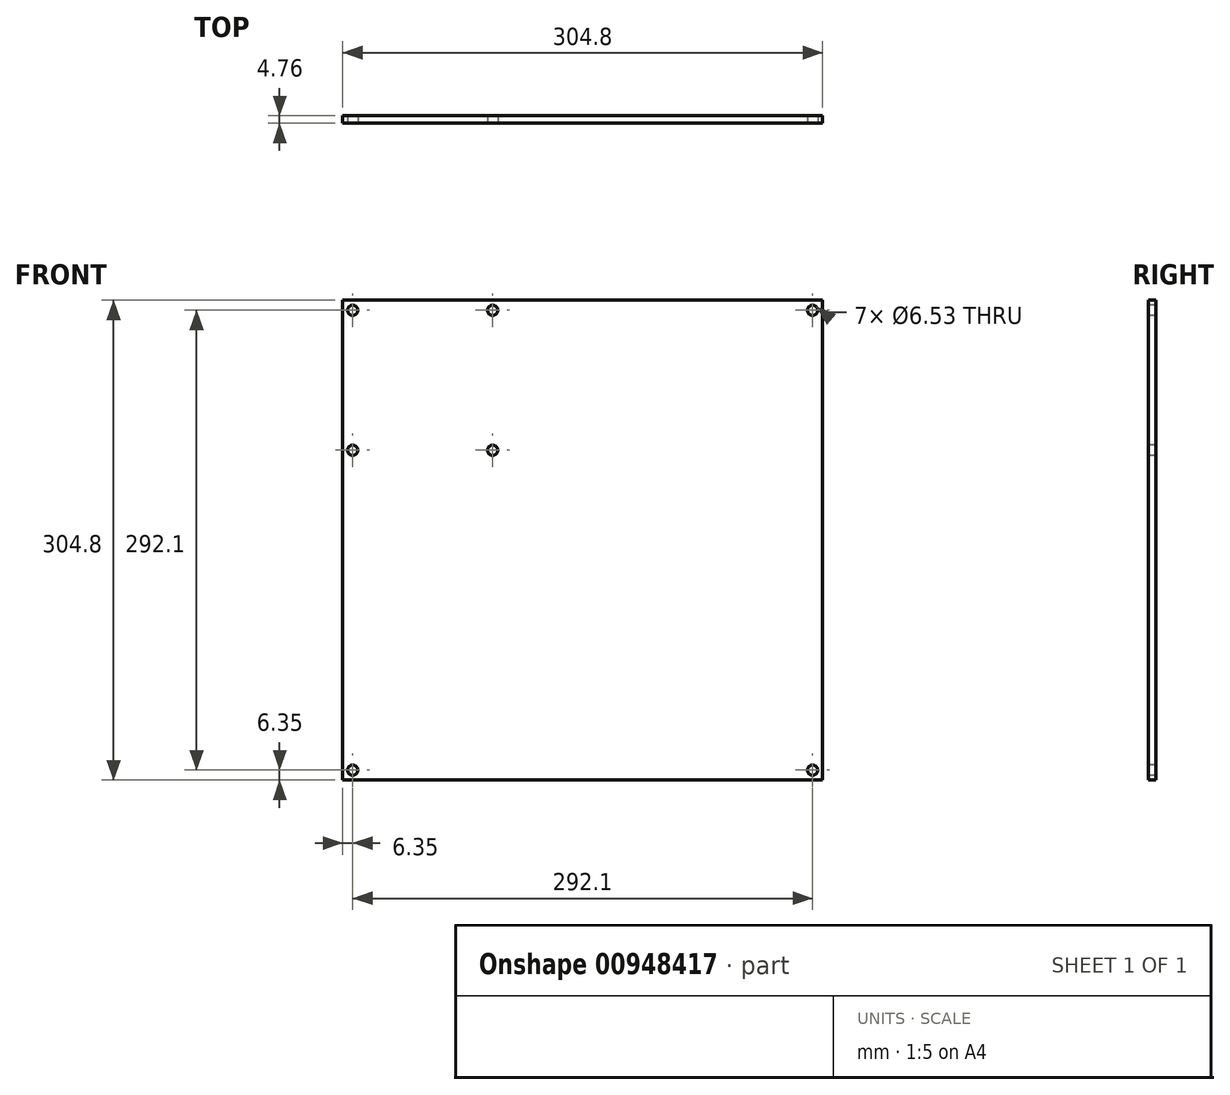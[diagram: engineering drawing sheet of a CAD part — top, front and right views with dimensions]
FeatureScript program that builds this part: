
annotation { "Feature Type Name" : "Feature", "Feature Type Description" : "" }
export const myFeature = defineFeature(function(context is Context, id is Id, definition is map)
    precondition{}
    {
        {
            var Q0;
            Q0=qCreatedBy(makeId("Front.planeOp"),FACE);
            var sketch = newSketch(context, id + "F0", { "sketchPlane" : qUnion([Q0])});
            skLineSegment(sketch, "E0.bottom", {"start": v(-152.4, 152.4) * mm, "end": v(152.4, 152.4) * mm});
            skLineSegment(sketch, "E0.top", {"start": v(-152.4, -152.4) * mm, "end": v(152.4, -152.4) * mm});
            skLineSegment(sketch, "E0.left", {"start": v(-152.4, 152.4) * mm, "end": v(-152.4, -152.4) * mm});
            skLineSegment(sketch, "E0.right", {"start": v(152.4, 152.4) * mm, "end": v(152.4, -152.4) * mm});
            skPoint(sketch, "E0.middle", {"position": v(0, 0) * mm});
            skLineSegment(sketch, "E1", {"start": v(0, 152.4) * mm, "end": v(0, -152.4) * mm, "construction": true});
            skLineSegment(sketch, "E2.bottom", {"start": v(-146.05, 146.05) * mm, "end": v(146.05, 146.05) * mm, "construction": true});
            skLineSegment(sketch, "E2.top", {"start": v(-146.05, -146.05) * mm, "end": v(146.05, -146.05) * mm, "construction": true});
            skLineSegment(sketch, "E2.left", {"start": v(-146.05, 146.05) * mm, "end": v(-146.05, -146.05) * mm, "construction": true});
            skLineSegment(sketch, "E2.right", {"start": v(146.05, 146.05) * mm, "end": v(146.05, -146.05) * mm, "construction": true});
            skLineSegment(sketch, "E3.bottom", {"start": v(-146.05, 146.05) * mm, "end": v(-57.15, 146.05) * mm});
            skLineSegment(sketch, "E3.top", {"start": v(-146.05, 57.15) * mm, "end": v(-57.15, 57.15) * mm});
            skLineSegment(sketch, "E3.left", {"start": v(-146.05, 146.05) * mm, "end": v(-146.05, 57.15) * mm});
            skLineSegment(sketch, "E3.right", {"start": v(-57.15, 146.05) * mm, "end": v(-57.15, 57.15) * mm});
            skPoint(sketch, "E3.middle", {"position": v(-101.6, 101.6) * mm});
            skCircle(sketch, "E4", {"center": v(-101.6, 101.6) * mm, "radius": 12.7 * mm});
            skSolve(sketch);
        }
        {
            var Q0;
            Q0=makeQuery(id+"F0.imprint","IMPRINT",FACE,{"disambiguationData":[TD([[makeQuery(id+"F0.imprint","IMPRINT",EDGE,{"derivedFrom":sQuery(id+"F0.wireOp",EDGE,"E0.bottom")}),-1.0]])]});
            var Q1;
            Q1=makeQuery(id+"F0.imprint","IMPRINT",FACE,{"disambiguationData":[TD([[makeQuery(id+"F0.imprint","IMPRINT",EDGE,{"derivedFrom":sQuery(id+"F0.wireOp",EDGE,"E3.bottom")}),-1.0]])]});
            var Q2;
            Q2=makeQuery(id+"F0.imprint","IMPRINT",FACE,{"disambiguationData":[TD([[makeQuery(id+"F0.imprint","IMPRINT",EDGE,{"derivedFrom":sQuery(id+"F0.wireOp",EDGE,"E4")}),1.0]])]});
            var Q3;
            Q3=sQuery(id+"F0.wireOp",EDGE,"E0.bottom");
            extrude(context, id + "F1", {"entities" : qUnion([Q0, Q1, Q2]), "surfaceEntities" : qUnion([Q3]), "oppositeDirection" : true, "depth" : 4.76 * mm, "offsetDistance" : 25.4 * mm});
        }
        {
            var Q0;
            Q0=sQuery(id+"F0.wireOp",VERTEX,"E2.bottom.start");
            var Q1;
            Q1=sQuery(id+"F0.wireOp",VERTEX,"E2.top.end");
            var Q2;
            Q2=sQuery(id+"F0.wireOp",VERTEX,"E2.bottom.end");
            var Q3;
            Q3=sQuery(id+"F0.wireOp",VERTEX,"E2.top.start");
            var Q4;
            Q4=makeQuery(id+"F1.opExtrude","SWEPT_BODY",BODY,{"disambiguationData":[OSD([sQuery(id+"F0.wireOp",EDGE,"E0.bottom"),sQuery(id+"F0.wireOp",EDGE,"E0.top"),sQuery(id+"F0.wireOp",EDGE,"E0.left"),sQuery(id+"F0.wireOp",EDGE,"E0.right")])]});
            hole(context, id + "F2", {"style" : HoleStyle.SIMPLE, "endStyle" : HoleEndStyle.THROUGH, "holeDiameter" : 6.53 * mm, "majorDiameter" : 6.35 * mm, "isTappedThrough" : true, "tappedDepth" : 12.7 * mm, "tapClearance" : 3, "locations" : qUnion([Q0, Q1, Q2, Q3]), "scope" : qUnion([Q4])});
        }
        {
            var Q0;
            Q0=sQuery(id+"F0.wireOp",VERTEX,"E3.bottom.start");
            var Q1;
            Q1=sQuery(id+"F0.wireOp",VERTEX,"E3.bottom.end");
            var Q2;
            Q2=sQuery(id+"F0.wireOp",VERTEX,"E3.top.end");
            var Q3;
            Q3=sQuery(id+"F0.wireOp",VERTEX,"E3.top.start");
            var Q4;
            Q4=makeQuery(id+"F1.opExtrude","SWEPT_BODY",BODY,{"disambiguationData":[OSD([sQuery(id+"F0.wireOp",EDGE,"E0.bottom"),sQuery(id+"F0.wireOp",EDGE,"E0.top"),sQuery(id+"F0.wireOp",EDGE,"E0.left"),sQuery(id+"F0.wireOp",EDGE,"E0.right")])]});
            hole(context, id + "F3", {"style" : HoleStyle.SIMPLE, "endStyle" : HoleEndStyle.THROUGH, "holeDiameter" : 6.53 * mm, "majorDiameter" : 6.35 * mm, "isTappedThrough" : true, "tappedDepth" : 12.7 * mm, "tapClearance" : 3, "locations" : qUnion([Q0, Q1, Q2, Q3]), "scope" : qUnion([Q4])});
        }
    });
